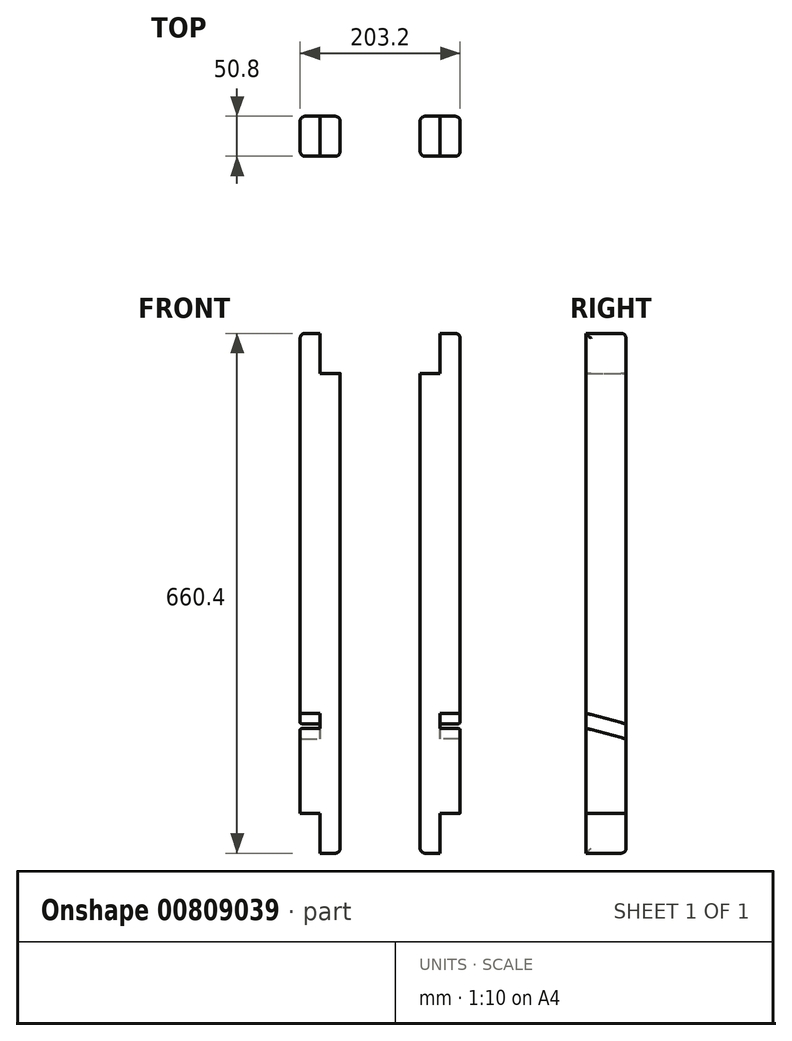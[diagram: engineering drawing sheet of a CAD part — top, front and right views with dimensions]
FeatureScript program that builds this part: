
annotation { "Feature Type Name" : "Feature", "Feature Type Description" : "" }
export const myFeature = defineFeature(function(context is Context, id is Id, definition is map)
    precondition{}
    {
        {
            var Q0;
            Q0=qCreatedBy(makeId("Top.planeOp"),FACE);
            var sketch = newSketch(context, id + "F0", { "sketchPlane" : qUnion([Q0])});
            skLineSegment(sketch, "E0.bottom", {"start": v(0, 0) * mm, "end": v(25.4, 0) * mm});
            skLineSegment(sketch, "E0.top", {"start": v(0, 50.8) * mm, "end": v(25.4, 50.8) * mm});
            skLineSegment(sketch, "E0.left", {"start": v(0, 0) * mm, "end": v(0, 50.8) * mm});
            skLineSegment(sketch, "E0.right", {"start": v(25.4, 0) * mm, "end": v(25.4, 50.8) * mm});
            skLineSegment(sketch, "E1.bottom", {"start": v(0, 0) * mm, "end": v(-25.4, 0) * mm});
            skLineSegment(sketch, "E1.top", {"start": v(0, 50.8) * mm, "end": v(-25.4, 50.8) * mm});
            skLineSegment(sketch, "E1.right", {"start": v(-25.4, 0) * mm, "end": v(-25.4, 50.8) * mm});
            skSolve(sketch);
        }
        {
            var Q0;
            Q0=makeQuery(id+"F0.imprint","IMPRINT",FACE,{"disambiguationData":[TD([[makeQuery(id+"F0.imprint","IMPRINT",EDGE,{"derivedFrom":sQuery(id+"F0.wireOp",EDGE,"E0.bottom")}),1.0]])]});
            extrude(context, id + "F1", {"entities" : qUnion([Q0]), "depth" : 609.6 * mm, "offsetDistance" : 25.4 * mm});
        }
        {
            var Q0;
            Q0=makeQuery(id+"F0.imprint","IMPRINT",FACE,{"disambiguationData":[TD([[makeQuery(id+"F0.imprint","IMPRINT",EDGE,{"derivedFrom":sQuery(id+"F0.wireOp",EDGE,"E1.bottom")}),-1.0]])]});
            extrude(context, id + "F2", {"entities" : qUnion([Q0]), "operationType" : NewBodyOperationType.ADD, "oppositeDirection" : true, "depth" : 50.8 * mm, "offsetDistance" : 25.4 * mm, "hasSecondDirection" : true, "secondDirectionOppositeDirection" : false, "secondDirectionDepth" : 558.8 * mm});
        }
        {
            var Q0;
            Q0=qCreatedBy(makeId("Right.planeOp"),FACE);
            var sketch = newSketch(context, id + "F3", { "sketchPlane" : qUnion([Q0])});
            skLineSegment(sketch, "E2", {"start": v(0, 107.95) * mm, "end": v(50.8, 94.34) * mm});
            skLineSegment(sketch, "E3", {"start": v(50.8, 94.34) * mm, "end": v(50.8, 113.39) * mm});
            skLineSegment(sketch, "E4", {"start": v(50.8, 113.39) * mm, "end": v(0, 127) * mm});
            skLineSegment(sketch, "E5", {"start": v(0, 127) * mm, "end": v(0, 107.95) * mm});
            skSolve(sketch);
        }
        {
            var Q0;
            Q0=qSketchRegion(id+"F3",true);
            extrude(context, id + "F4", {"entities" : qUnion([Q0]), "operationType" : NewBodyOperationType.REMOVE, "depth" : 25.4 * mm, "offsetDistance" : 25.4 * mm});
        }
        {
            var Q0;
            {var subQ0=sQuery(id+"F0.wireOp",EDGE,"E0.right");var subQ1=sQuery(id+"F0.wireOp",EDGE,"E0.top");Q0=makeQuery(id+"F4.boolean.opBoolean","SPLIT",EDGE,{"disambiguationData":[TD([makeQuery(id+"F4.opExtrude","SWEPT_FACE",FACE,{"disambiguationData":[OSD([sQuery(id+"F3.wireOp",EDGE,"E2")])]})])],"derivedFrom":makeQuery(id+"F1.opExtrude","SWEPT_EDGE",EDGE,{"disambiguationData":[OSD([subQ1,subQ0])]})});}
            var Q1;
            {var subQ0=sQuery(id+"F0.wireOp",EDGE,"E0.right");var subQ1=sQuery(id+"F0.wireOp",EDGE,"E0.top");Q1=makeQuery(id+"F4.boolean.opBoolean","SPLIT",EDGE,{"disambiguationData":[TD([makeQuery(id+"F4.opExtrude","SWEPT_FACE",FACE,{"disambiguationData":[OSD([sQuery(id+"F3.wireOp",EDGE,"E4")])]})])],"derivedFrom":makeQuery(id+"F1.opExtrude","SWEPT_EDGE",EDGE,{"disambiguationData":[OSD([subQ1,subQ0])]})});}
            var Q2;
            Q2=makeQuery(id+"F2.opExtrude","SWEPT_EDGE",EDGE,{"disambiguationData":[OSD([sQuery(id+"F0.wireOp",EDGE,"E1.top"),sQuery(id+"F0.wireOp",EDGE,"E1.right")])]});
            var Q3;
            Q3=makeQuery(id+"F2.opExtrude","CAP_EDGE",EDGE,{"disambiguationData":[OSD([sQuery(id+"F0.wireOp",EDGE,"E1.top")])],"isStart":false});
            var Q4;
            Q4=makeQuery(id+"F2.opExtrude","CAP_EDGE",EDGE,{"disambiguationData":[OSD([sQuery(id+"F0.wireOp",EDGE,"E1.right")])],"isStart":false});
            var Q5;
            Q5=makeQuery(id+"F2.opExtrude","SWEPT_EDGE",EDGE,{"disambiguationData":[OSD([sQuery(id+"F0.wireOp",EDGE,"E1.bottom"),sQuery(id+"F0.wireOp",EDGE,"E1.right")])]});
            var Q6;
            Q6=makeQuery(id+"F1.opExtrude","CAP_EDGE",EDGE,{"disambiguationData":[OSD([sQuery(id+"F0.wireOp",EDGE,"E0.top")])],"isStart":false});
            var Q7;
            Q7=makeQuery(id+"F1.opExtrude","CAP_EDGE",EDGE,{"disambiguationData":[OSD([sQuery(id+"F0.wireOp",EDGE,"E0.right")])],"isStart":false});
            var Q8;
            {var subQ0=sQuery(id+"F0.wireOp",EDGE,"E0.right");var subQ1=sQuery(id+"F0.wireOp",EDGE,"E0.bottom");Q8=makeQuery(id+"F4.boolean.opBoolean","SPLIT",EDGE,{"disambiguationData":[TD([makeQuery(id+"F4.opExtrude","SWEPT_FACE",FACE,{"disambiguationData":[OSD([sQuery(id+"F3.wireOp",EDGE,"E4")])]})])],"derivedFrom":makeQuery(id+"F1.opExtrude","SWEPT_EDGE",EDGE,{"disambiguationData":[OSD([subQ1,subQ0])]})});}
            var Q9;
            {var subQ0=sQuery(id+"F0.wireOp",EDGE,"E0.right");var subQ1=sQuery(id+"F0.wireOp",EDGE,"E0.bottom");Q9=makeQuery(id+"F4.boolean.opBoolean","SPLIT",EDGE,{"disambiguationData":[TD([makeQuery(id+"F4.opExtrude","SWEPT_FACE",FACE,{"disambiguationData":[OSD([sQuery(id+"F3.wireOp",EDGE,"E2")])]})])],"derivedFrom":makeQuery(id+"F1.opExtrude","SWEPT_EDGE",EDGE,{"disambiguationData":[OSD([subQ1,subQ0])]})});}
            fillet(context, id + "F5", {"entities" : qUnion([Q0, Q1, Q2, Q3, Q4, Q5, Q6, Q7, Q8, Q9]), "radius" : 6.35 * mm, "tangentPropagation" : true, "allowEdgeOverflow" : false});
        }
        {
            var Q0;
            Q0=qCreatedBy(makeId("Right.planeOp"),FACE);
            cPlane(context, id + "F6", {"entities" : qUnion([Q0]), "cplaneType" : CPlaneType.OFFSET, "offset" : 76.2 * mm, "oppositeDirection" : true, "width" : 152.4 * mm, "height" : 152.4 * mm});
        }
        {
            var Q0;
            Q0=makeQuery(id+"F1.opExtrude","SWEPT_BODY",BODY,{"disambiguationData":[OSD([sQuery(id+"F0.wireOp",EDGE,"E0.bottom"),sQuery(id+"F0.wireOp",EDGE,"E0.top"),sQuery(id+"F0.wireOp",EDGE,"E0.right"),sQuery(id+"F0.wireOp",EDGE,"E0.left")])]});
            var Q1;
            Q1=qCreatedBy(id+"F6.planeOp",FACE);
            mirror(context, id + "F7", {"entities" : qUnion([Q0]), "mirrorPlane" : qUnion([Q1])});
        }
    });
